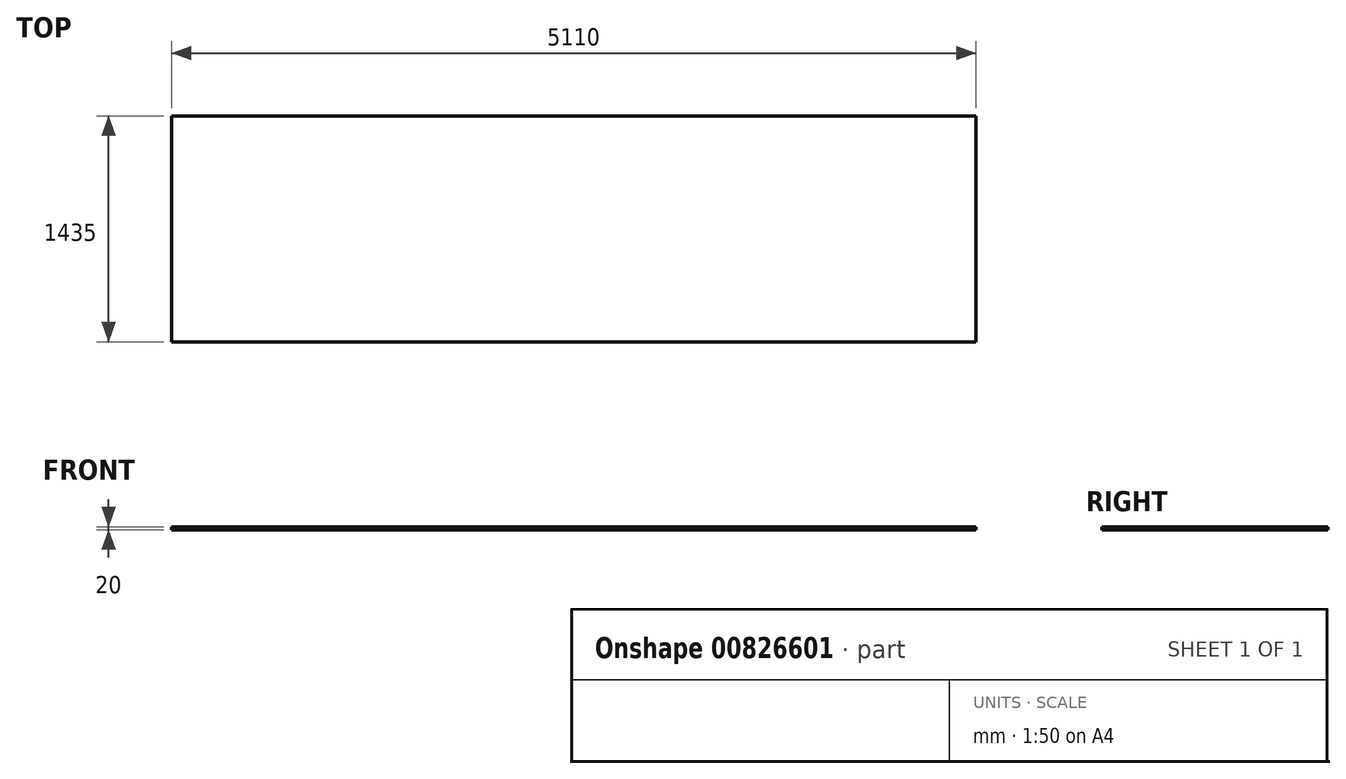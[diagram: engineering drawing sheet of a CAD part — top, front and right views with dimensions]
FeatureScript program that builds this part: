
annotation { "Feature Type Name" : "Feature", "Feature Type Description" : "" }
export const myFeature = defineFeature(function(context is Context, id is Id, definition is map)
    precondition{}
    {
        {
            var Q0;
            Q0=qCreatedBy(makeId("Top.planeOp"),FACE);
            var sketch = newSketch(context, id + "F0", { "sketchPlane" : qUnion([Q0])});
            skLineSegment(sketch, "E0.bottom", {"start": v(-2511.17, 359.85) * mm, "end": v(2598.83, 359.85) * mm});
            skLineSegment(sketch, "E0.top", {"start": v(-2511.17, -1075.15) * mm, "end": v(2598.83, -1075.15) * mm});
            skLineSegment(sketch, "E0.left", {"start": v(-2511.17, 359.85) * mm, "end": v(-2511.17, -1075.15) * mm});
            skLineSegment(sketch, "E0.right", {"start": v(2598.83, 359.85) * mm, "end": v(2598.83, -1075.15) * mm});
            skSolve(sketch);
        }
        {
            var Q0;
            Q0=makeQuery(id+"F0.imprint","IMPRINT",FACE,{"disambiguationData":[TD([[makeQuery(id+"F0.imprint","IMPRINT",EDGE,{"derivedFrom":sQuery(id+"F0.wireOp",EDGE,"E0.bottom")}),-1.0]])]});
            var sketch = newSketch(context, id + "F1", { "sketchPlane" : qUnion([Q0])});
            skSolve(sketch);
        }
        {
            var Q0;
            Q0=makeQuery(id+"F1.imprint","IMPRINT",FACE,{"disambiguationData":[TD([[makeQuery(id+"F1.imprint","IMPRINT",EDGE,{"derivedFrom":makeQuery(id+"F0.imprint","IMPRINT",EDGE,{"derivedFrom":sQuery(id+"F0.wireOp",EDGE,"E0.bottom")})}),-1.0]])]});
            extrude(context, id + "F2", {"entities" : qUnion([Q0]), "depth" : 20 * mm, "offsetDistance" : 25 * mm});
        }
    });
